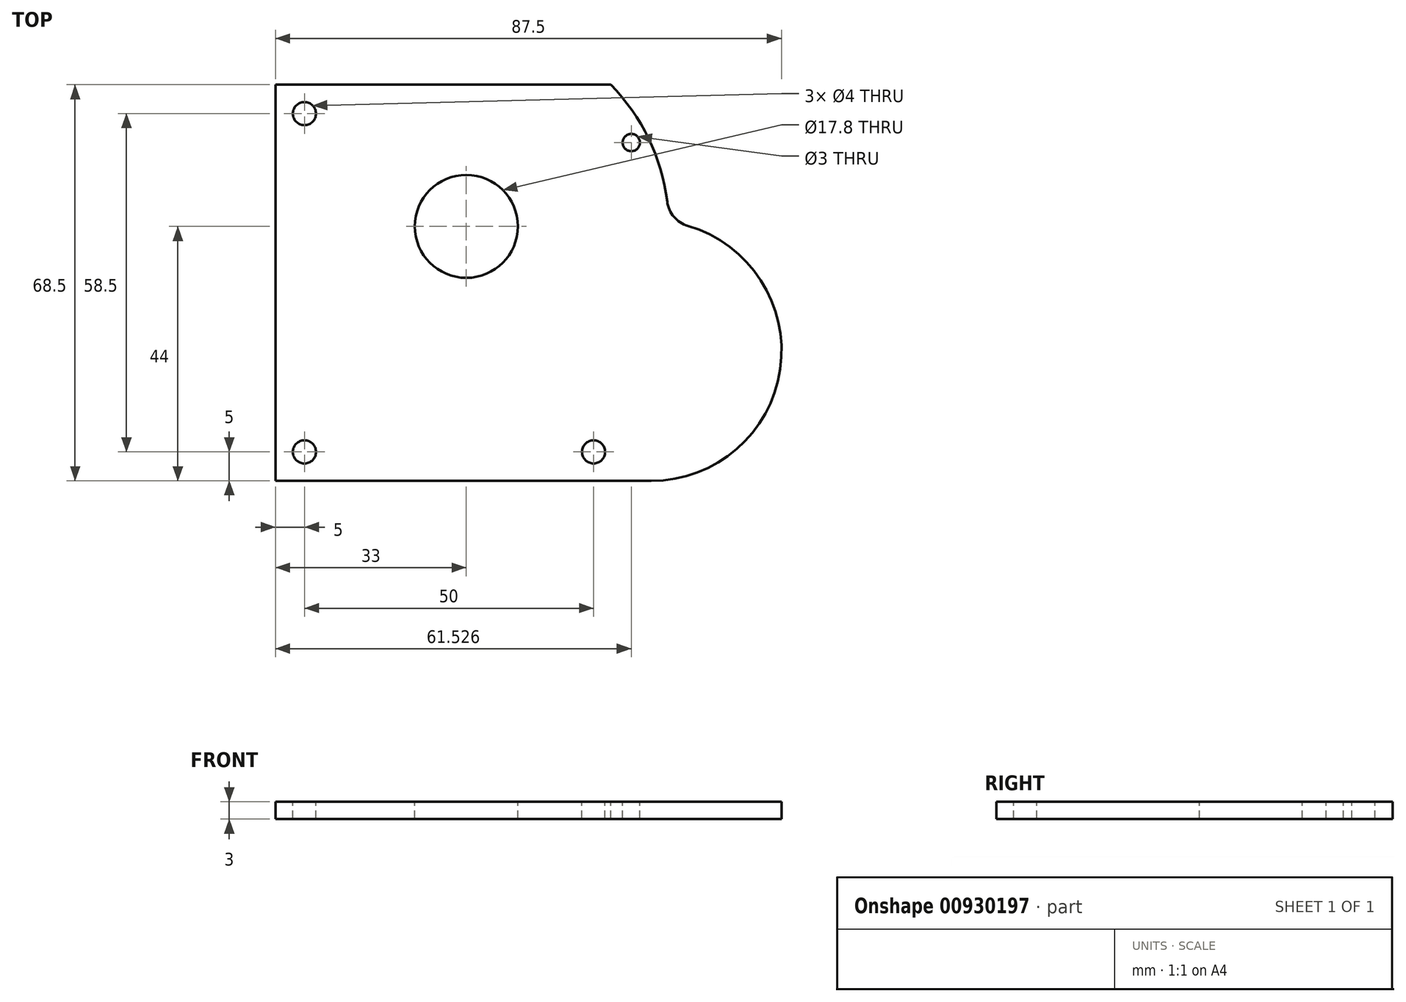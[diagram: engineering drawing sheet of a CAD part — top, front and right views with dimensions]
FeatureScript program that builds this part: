
annotation { "Feature Type Name" : "Feature", "Feature Type Description" : "" }
export const myFeature = defineFeature(function(context is Context, id is Id, definition is map)
    precondition{}
    {
        {
            var Q0;
            Q0=qCreatedBy(makeId("Top.planeOp"),FACE);
            var sketch = newSketch(context, id + "F0", { "sketchPlane" : qUnion([Q0])});
            skLineSegment(sketch, "E0.bottom", {"start": v(50, 34.25) * mm, "end": v(-50, 34.25) * mm});
            skLineSegment(sketch, "E0.top", {"start": v(50, -34.25) * mm, "end": v(-50, -34.25) * mm});
            skLineSegment(sketch, "E0.left", {"start": v(50, 34.25) * mm, "end": v(50, -34.25) * mm});
            skLineSegment(sketch, "E0.right", {"start": v(-50, 34.25) * mm, "end": v(-50, -34.25) * mm});
            skPoint(sketch, "E0.middle", {"position": v(0, 0) * mm});
            skSolve(sketch);
        }
        {
            var Q0;
            Q0=makeQuery(id+"F0.imprint","IMPRINT",FACE,{"disambiguationData":[TD([[makeQuery(id+"F0.imprint","IMPRINT",EDGE,{"derivedFrom":sQuery(id+"F0.wireOp",EDGE,"E0.bottom")}),1.0]])]});
            extrude(context, id + "F1", {"entities" : qUnion([Q0]), "depth" : 3 * mm, "offsetDistance" : 25 * mm});
        }
        {
            var Q0;
            Q0=makeQuery(id+"F1.opExtrude","CAP_FACE",FACE,{"disambiguationData":[OSD([sQuery(id+"F0.wireOp",EDGE,"E0.bottom"),sQuery(id+"F0.wireOp",EDGE,"E0.top"),sQuery(id+"F0.wireOp",EDGE,"E0.left"),sQuery(id+"F0.wireOp",EDGE,"E0.right")])],"isStart":false});
            var sketch = newSketch(context, id + "F2", { "sketchPlane" : qUnion([Q0])});
            skLineSegment(sketch, "E1.0", {"start": v(50, 34.25) * mm, "end": v(-50, 34.25) * mm});
            skLineSegment(sketch, "E2.0", {"start": v(50, 34.25) * mm, "end": v(50, -34.25) * mm});
            skLineSegment(sketch, "E3.0", {"start": v(50, -34.25) * mm, "end": v(-50, -34.25) * mm});
            skLineSegment(sketch, "E4", {"start": v(-65.3, 0) * mm, "end": v(74.93, 0) * mm, "construction": true});
            skLineSegment(sketch, "E5", {"start": v(0, 54.73) * mm, "end": v(0, -46.56) * mm, "construction": true});
            skPoint(sketch, "E5.endSnap0", {"position": v(0, -34.25) * mm});
            skCircle(sketch, "E6", {"center": v(-17, 9.75) * mm, "radius": 35 * mm, "construction": true});
            skCircle(sketch, "E7", {"center": v(15, -11.75) * mm, "radius": 22.5 * mm, "construction": true});
            skPoint(sketch, "E8", {"position": v(18, 10.55) * mm});
            skPoint(sketch, "E9", {"position": v(15, -34.25) * mm});
            skArc(sketch, "E10", {"start": v(15, -34.25) * mm, "mid": v(37.45, -13.25) * mm, "end": v(18, 10.55) * mm});
            skLineSegment(sketch, "E11", {"start": v(-50, -34.25) * mm, "end": v(15, -34.25) * mm});
            skCircle(sketch, "E12", {"center": v(-17, 9.75) * mm, "radius": 8.9 * mm});
            skPoint(sketch, "E13", {"position": v(8, 34.25) * mm});
            skArc(sketch, "E14", {"start": v(18, 10.55) * mm, "mid": v(15.25, 23.35) * mm, "end": v(8, 34.25) * mm});
            skSolve(sketch);
        }
        {
            var Q0;
            Q0=makeQuery(id+"F2.imprint","IMPRINT",FACE,{"disambiguationData":[TD([[makeQuery(id+"F2.imprint","IMPRINT",EDGE,{"derivedFrom":sQuery(id+"F2.wireOp",EDGE,"E1.0")}),1.0]])]});
            var Q1;
            Q1=makeQuery(id+"F2.imprint","IMPRINT",FACE,{"disambiguationData":[TD([[makeQuery(id+"F2.imprint","IMPRINT",EDGE,{"derivedFrom":sQuery(id+"F2.wireOp",EDGE,"E12")}),1.0]])]});
            extrude(context, id + "F3", {"entities" : qUnion([Q0, Q1]), "operationType" : NewBodyOperationType.REMOVE, "endBound" : BoundingType.THROUGH_ALL, "oppositeDirection" : true, "depth" : 25 * mm, "offsetDistance" : 25 * mm});
        }
        {
            var Q0;
            Q0=makeQuery(id+"F3.boolean.opBoolean","COPY",EDGE,{"derivedFrom":makeQuery(id+"F3.opExtrude","SWEPT_EDGE",EDGE,{"disambiguationData":[OSD([sQuery(id+"F2.wireOp",EDGE,"k0z0n1ct-9dLm-HaFo-13mC-3Y1S7aB4fgMI"),sQuery(id+"F2.wireOp",EDGE,"E10")])]})});
            fillet(context, id + "F4", {"entities" : qUnion([Q0]), "radius" : 5 * mm, "tangentPropagation" : true, "allowEdgeOverflow" : false});
        }
        {
            var Q0;
            Q0=makeQuery(id+"F1.opExtrude","CAP_FACE",FACE,{"disambiguationData":[OSD([sQuery(id+"F0.wireOp",EDGE,"E0.bottom"),sQuery(id+"F0.wireOp",EDGE,"E0.top"),sQuery(id+"F0.wireOp",EDGE,"E0.left"),sQuery(id+"F0.wireOp",EDGE,"E0.right")])],"isStart":false});
            var sketch = newSketch(context, id + "F5", { "sketchPlane" : qUnion([Q0])});
            skLineSegment(sketch, "E15.0", {"start": v(8, 34.25) * mm, "end": v(-50, 34.25) * mm});
            skLineSegment(sketch, "E16.0", {"start": v(-50, 34.25) * mm, "end": v(-50, -34.25) * mm});
            skLineSegment(sketch, "E17.0", {"start": v(15, -34.25) * mm, "end": v(-50, -34.25) * mm});
            skArc(sketch, "E18.0", {"start": v(15, -34.25) * mm, "mid": v(37.27, -14.93) * mm, "end": v(21.3, 9.85) * mm});
            skArc(sketch, "E19.0", {"start": v(17.74, 14.04) * mm, "mid": v(14.53, 24.95) * mm, "end": v(8, 34.25) * mm});
            skCircle(sketch, "E20", {"center": v(11.53, 24.25) * mm, "radius": 1.5 * mm});
            skCircle(sketch, "E21", {"center": v(5, -29.25) * mm, "radius": 2 * mm});
            skCircle(sketch, "E22", {"center": v(-45, 29.25) * mm, "radius": 2 * mm});
            skCircle(sketch, "E23", {"center": v(-45, -29.25) * mm, "radius": 2 * mm});
            skSolve(sketch);
        }
        {
            var Q0;
            Q0=makeQuery(id+"F5.imprint","IMPRINT",FACE,{"disambiguationData":[TD([[makeQuery(id+"F5.imprint","IMPRINT",EDGE,{"derivedFrom":sQuery(id+"F5.wireOp",EDGE,"E22")}),1.0]])]});
            var Q1;
            Q1=makeQuery(id+"F5.imprint","IMPRINT",FACE,{"disambiguationData":[TD([[makeQuery(id+"F5.imprint","IMPRINT",EDGE,{"derivedFrom":sQuery(id+"F5.wireOp",EDGE,"E20")}),1.0]])]});
            var Q2;
            Q2=makeQuery(id+"F5.imprint","IMPRINT",FACE,{"disambiguationData":[TD([[makeQuery(id+"F5.imprint","IMPRINT",EDGE,{"derivedFrom":sQuery(id+"F5.wireOp",EDGE,"E23")}),1.0]])]});
            var Q3;
            Q3=makeQuery(id+"F5.imprint","IMPRINT",FACE,{"disambiguationData":[TD([[makeQuery(id+"F5.imprint","IMPRINT",EDGE,{"derivedFrom":sQuery(id+"F5.wireOp",EDGE,"E21")}),1.0]])]});
            extrude(context, id + "F6", {"entities" : qUnion([Q0, Q1, Q2, Q3]), "operationType" : NewBodyOperationType.REMOVE, "endBound" : BoundingType.THROUGH_ALL, "oppositeDirection" : true, "depth" : 25 * mm, "offsetDistance" : 25 * mm});
        }
    });
